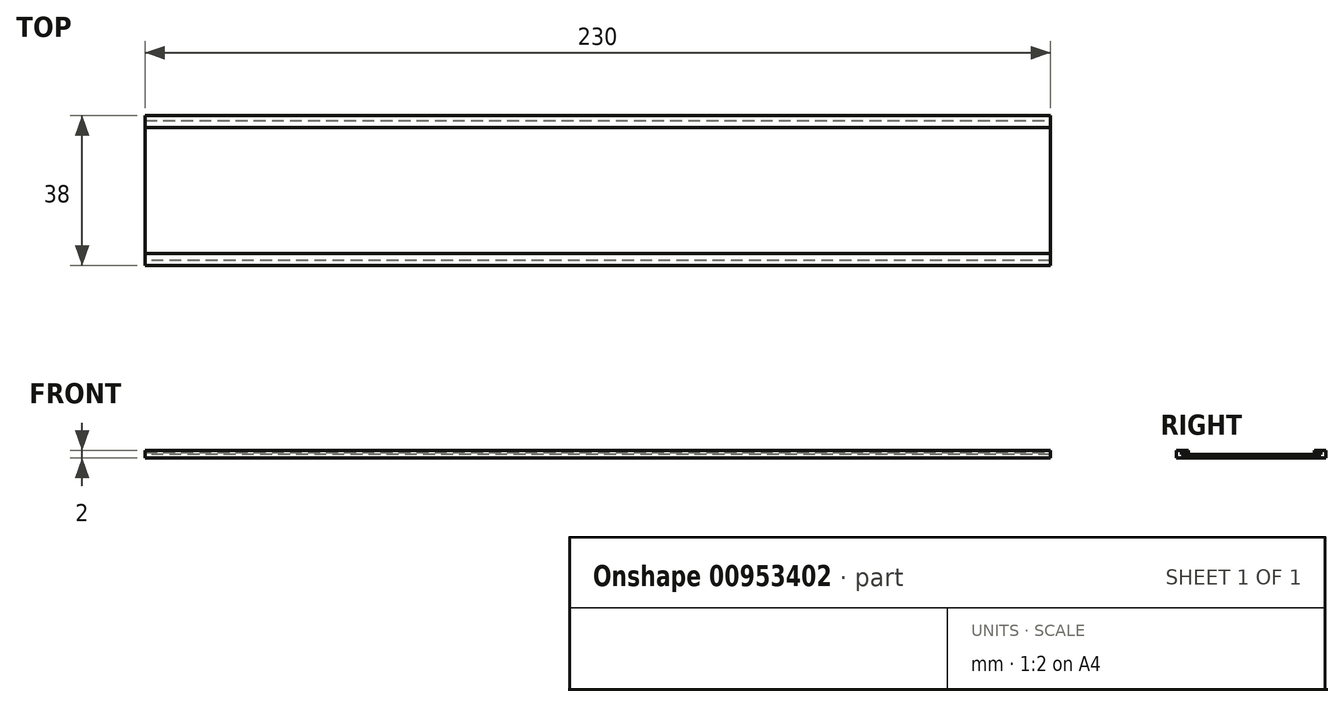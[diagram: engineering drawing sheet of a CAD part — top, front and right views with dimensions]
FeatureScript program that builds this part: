
annotation { "Feature Type Name" : "Feature", "Feature Type Description" : "" }
export const myFeature = defineFeature(function(context is Context, id is Id, definition is map)
    precondition{}
    {
        {
            var Q0;
            Q0=qCreatedBy(makeId("Top.planeOp"),FACE);
            var sketch = newSketch(context, id + "F0", { "sketchPlane" : qUnion([Q0])});
            skLineSegment(sketch, "E0.bottom", {"start": v(115, 19) * mm, "end": v(-115, 19) * mm});
            skLineSegment(sketch, "E0.top", {"start": v(115, -19) * mm, "end": v(-115, -19) * mm});
            skLineSegment(sketch, "E0.left", {"start": v(115, 19) * mm, "end": v(115, -19) * mm});
            skLineSegment(sketch, "E0.right", {"start": v(-115, 19) * mm, "end": v(-115, -19) * mm});
            skPoint(sketch, "E0.middle", {"position": v(0, 0) * mm});
            skSolve(sketch);
        }
        {
            var Q0;
            Q0 = qSketchRegion(id + "F0", true);
            extrude(context, id + "F1", {"entities" : qUnion([Q0]), "depth" : 1 * mm, "offsetDistance" : 25.4 * mm});
        }
        {
            var Q0;
            Q0=makeQuery(id+"F1.opExtrude","CAP_FACE",FACE,{"disambiguationData":[OSD([sQuery(id+"F0.wireOp",EDGE,"E0.bottom"),sQuery(id+"F0.wireOp",EDGE,"E0.top"),sQuery(id+"F0.wireOp",EDGE,"E0.left"),sQuery(id+"F0.wireOp",EDGE,"E0.right")])],"isStart":false});
            var sketch = newSketch(context, id + "F2", { "sketchPlane" : qUnion([Q0])});
            skLineSegment(sketch, "E1.bottom", {"start": v(-115, 19) * mm, "end": v(115, 19) * mm});
            skLineSegment(sketch, "E1.top", {"start": v(-115, 17.75) * mm, "end": v(115, 17.75) * mm});
            skLineSegment(sketch, "E1.left", {"start": v(-115, 19) * mm, "end": v(-115, 17.75) * mm});
            skLineSegment(sketch, "E1.right", {"start": v(115, 19) * mm, "end": v(115, 17.75) * mm});
            skLineSegment(sketch, "E2.MirrorCS", {"start": v(115, 19) * mm, "end": v(-115, 19) * mm});
            skLineSegment(sketch, "E3.MirrorCS", {"start": v(115, 17.75) * mm, "end": v(-115, 17.75) * mm});
            skLineSegment(sketch, "E4.MirrorCS", {"start": v(115, -19) * mm, "end": v(115, -17.75) * mm});
            skLineSegment(sketch, "E5.MirrorCS", {"start": v(-115, -19) * mm, "end": v(-115, -17.75) * mm});
            skLineSegment(sketch, "E6.MirrorCS", {"start": v(-115, -19) * mm, "end": v(115, -19) * mm});
            skLineSegment(sketch, "E7.MirrorCS", {"start": v(115, -19) * mm, "end": v(-115, -19) * mm});
            skLineSegment(sketch, "E8.MirrorCS", {"start": v(115, -17.75) * mm, "end": v(-115, -17.75) * mm});
            skLineSegment(sketch, "E9.MirrorCS", {"start": v(-115, -17.75) * mm, "end": v(115, -17.75) * mm});
            skSolve(sketch);
        }
        {
            var Q0;
            Q0 = qSketchRegion(id + "F2", true);
            extrude(context, id + "F3", {"entities" : qUnion([Q0]), "operationType" : NewBodyOperationType.ADD, "depth" : .5 * mm, "offsetDistance" : 25 * mm});
        }
        {
            var Q0;
            Q0=makeQuery(id+"F3.opExtrude","CAP_FACE",FACE,{"disambiguationData":[OSD([sQuery(id+"F2.wireOp",EDGE,"E1.right"),sQuery(id+"F2.wireOp",EDGE,"E1.left"),sQuery(id+"F2.wireOp",EDGE,"E2.MirrorCS"),sQuery(id+"F2.wireOp",EDGE,"E1.top")])],"isStart":false});
            var sketch = newSketch(context, id + "F4", { "sketchPlane" : qUnion([Q0])});
            skLineSegment(sketch, "E10.bottom", {"start": v(-115, 19) * mm, "end": v(115, 19) * mm});
            skLineSegment(sketch, "E10.top", {"start": v(-115, 16) * mm, "end": v(115, 16) * mm});
            skLineSegment(sketch, "E10.left", {"start": v(-115, 19) * mm, "end": v(-115, 16) * mm});
            skLineSegment(sketch, "E10.right", {"start": v(115, 19) * mm, "end": v(115, 16) * mm});
            skLineSegment(sketch, "E11.MirrorCS", {"start": v(115, -19) * mm, "end": v(115, -16) * mm});
            skLineSegment(sketch, "E12.MirrorCS", {"start": v(-115, -19) * mm, "end": v(-115, -16) * mm});
            skLineSegment(sketch, "E13.MirrorCS", {"start": v(-115, -16) * mm, "end": v(115, -16) * mm});
            skLineSegment(sketch, "E14.MirrorCS", {"start": v(-115, -19) * mm, "end": v(115, -19) * mm});
            skSolve(sketch);
        }
        {
            var Q0;
            Q0 = qSketchRegion(id + "F4", true);
            extrude(context, id + "F5", {"entities" : qUnion([Q0]), "operationType" : NewBodyOperationType.ADD, "depth" : .5 * mm, "offsetDistance" : 25 * mm});
        }
    });
